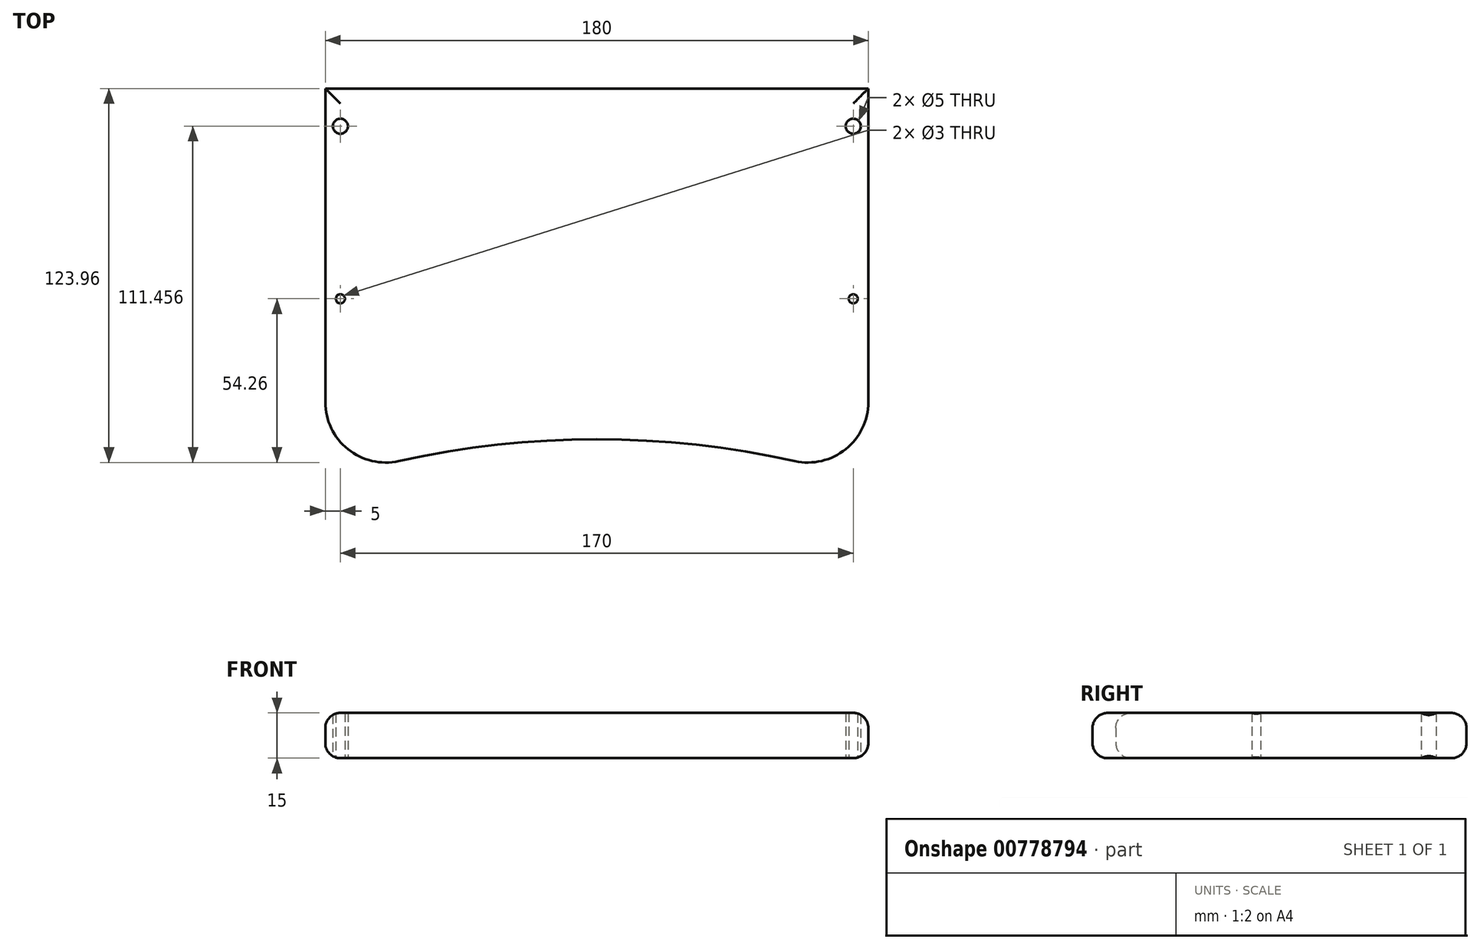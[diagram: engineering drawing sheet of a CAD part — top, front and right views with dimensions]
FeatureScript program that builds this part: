
annotation { "Feature Type Name" : "Feature", "Feature Type Description" : "" }
export const myFeature = defineFeature(function(context is Context, id is Id, definition is map)
    precondition{}
    {
        {
            var Q0;
            Q0=qCreatedBy(makeId("Top.planeOp"),FACE);
            var sketch = newSketch(context, id + "F0", { "sketchPlane" : qUnion([Q0])});
            skLineSegment(sketch, "E0", {"start": v(-90, 69.7) * mm, "end": v(-90, -34.26) * mm});
            skLineSegment(sketch, "E1", {"start": v(-90, 69.7) * mm, "end": v(90, 69.7) * mm});
            skLineSegment(sketch, "E2", {"start": v(90, 69.7) * mm, "end": v(90, -34.26) * mm});
            skArc(sketch, "E3", {"start": v(65.64, -53.78) * mm, "mid": v(0, -46.54) * mm, "end": v(-65.64, -53.78) * mm});
            skPoint(sketch, "E4.visualSharp", {"position": v(-90, -60.3) * mm});
            skArc(sketch, "E4.filletArc", {"start": v(-90, -34.26) * mm, "mid": v(-82.5, -49.87) * mm, "end": v(-65.64, -53.78) * mm});
            skPoint(sketch, "E5.visualSharp", {"position": v(90, -60.3) * mm});
            skArc(sketch, "E5.filletArc", {"start": v(65.64, -53.78) * mm, "mid": v(82.5, -49.87) * mm, "end": v(90, -34.26) * mm});
            skCircle(sketch, "E6", {"center": v(-85, 57.2) * mm, "radius": 2.5 * mm});
            skCircle(sketch, "E7", {"center": v(-85, 0) * mm, "radius": 1.5 * mm});
            skCircle(sketch, "E8", {"center": v(85, 57.2) * mm, "radius": 2.5 * mm});
            skCircle(sketch, "E9", {"center": v(85, 0) * mm, "radius": 1.5 * mm});
            skSolve(sketch);
        }
        {
            var Q0;
            Q0=makeQuery(id+"F0.imprint","IMPRINT",FACE,{"disambiguationData":[TD([[makeQuery(id+"F0.imprint","IMPRINT",EDGE,{"derivedFrom":sQuery(id+"F0.wireOp",EDGE,"E0")}),1.0]])]});
            extrude(context, id + "F1", {"entities" : qUnion([Q0]), "depth" : 15 * mm, "offsetDistance" : 25 * mm});
        }
        {
            var Q0;
            Q0=makeQuery(id+"F1.opExtrude","CAP_EDGE",EDGE,{"disambiguationData":[OSD([sQuery(id+"F0.wireOp",EDGE,"E0")])],"isStart":false});
            var Q1;
            Q1=makeQuery(id+"F1.opExtrude","CAP_EDGE",EDGE,{"disambiguationData":[OSD([sQuery(id+"F0.wireOp",EDGE,"E1")])],"isStart":false});
            fillet(context, id + "F2", {"entities" : qUnion([Q0, Q1]), "radius" : 5 * mm, "tangentPropagation" : true, "allowEdgeOverflow" : false});
        }
        {
            var Q0;
            Q0=makeQuery(id+"F1.opExtrude","CAP_EDGE",EDGE,{"disambiguationData":[OSD([sQuery(id+"F0.wireOp",EDGE,"E1")])],"isStart":true});
            var Q1;
            Q1=makeQuery(id+"F1.opExtrude","CAP_EDGE",EDGE,{"disambiguationData":[OSD([sQuery(id+"F0.wireOp",EDGE,"E0")])],"isStart":true});
            fillet(context, id + "F3", {"entities" : qUnion([Q0, Q1]), "radius" : 5 * mm, "tangentPropagation" : true, "allowEdgeOverflow" : false});
        }
    });
